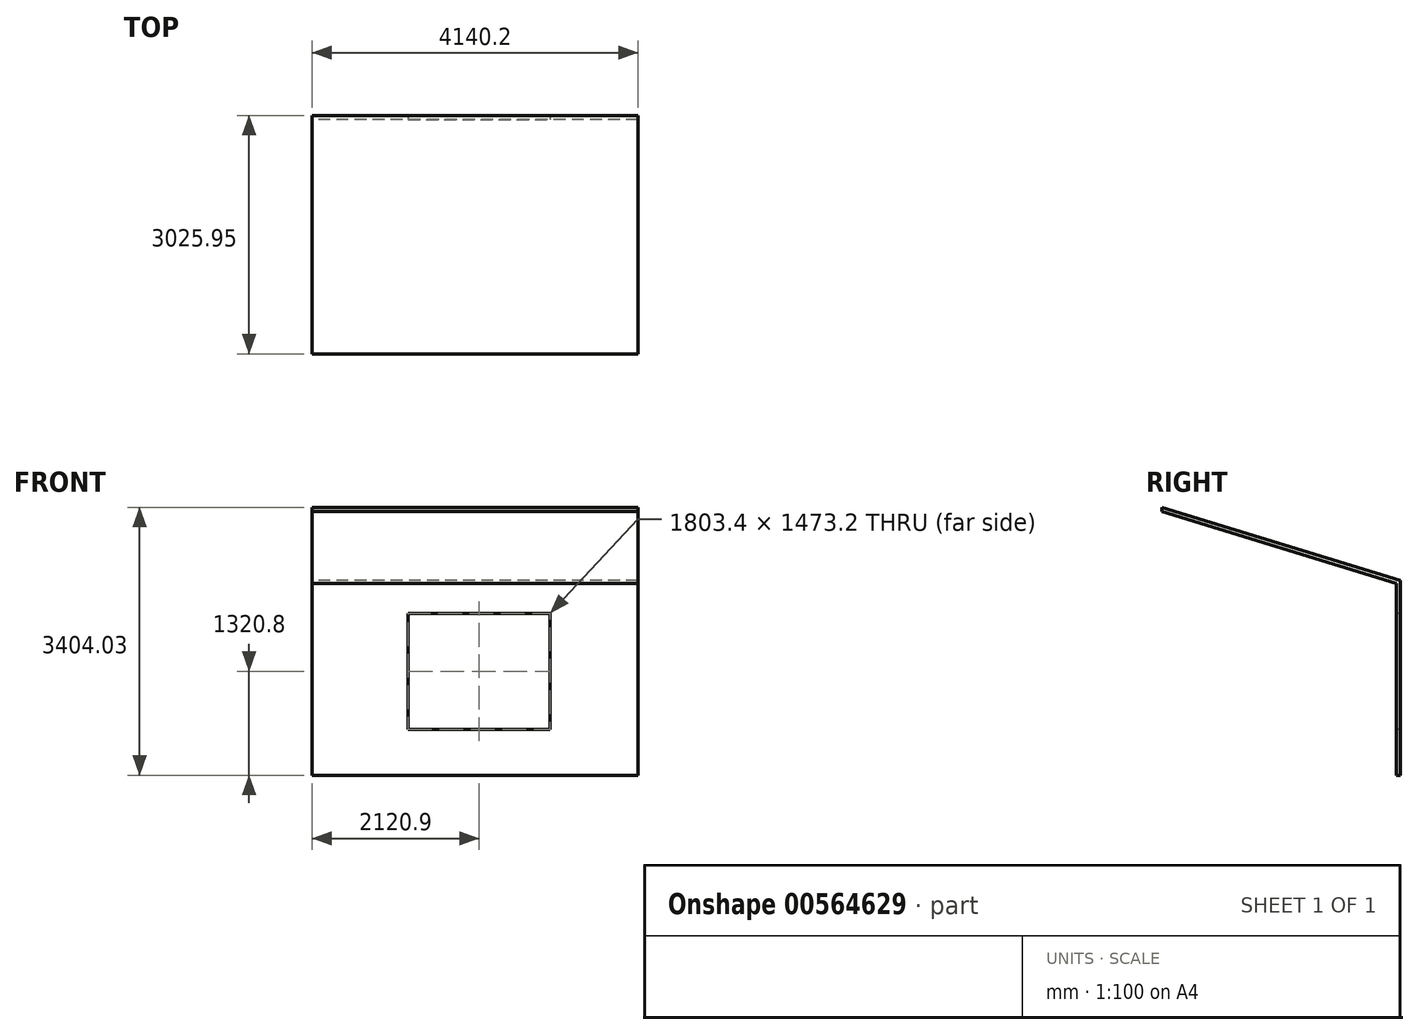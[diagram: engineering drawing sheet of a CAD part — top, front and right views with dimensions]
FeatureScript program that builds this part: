
annotation { "Feature Type Name" : "Feature", "Feature Type Description" : "" }
export const myFeature = defineFeature(function(context is Context, id is Id, definition is map)
    precondition{}
    {
        {
            var Q0;
            Q0=qCreatedBy(makeId("Right.planeOp"),FACE);
            var sketch = newSketch(context, id + "F0", { "sketchPlane" : qUnion([Q0])});
            skLineSegment(sketch, "E0", {"start": v(0, 0) * mm, "end": v(0, 2438.4) * mm});
            skLineSegment(sketch, "E1", {"start": v(0, 2438.4) * mm, "end": v(-2975.15, 3353.23) * mm});
            skLineSegment(sketch, "E2", {"start": v(-2975.15, 3353.23) * mm, "end": v(-2975.15, 3404.03) * mm});
            skLineSegment(sketch, "E3", {"start": v(-2975.15, 3404.03) * mm, "end": v(50.8, 2473.58) * mm});
            skLineSegment(sketch, "E4", {"start": v(50.8, 2473.58) * mm, "end": v(50.8, 0) * mm});
            skLineSegment(sketch, "E5", {"start": v(50.8, 0) * mm, "end": v(0, 0) * mm});
            skSolve(sketch);
        }
        {
            var Q0;
            Q0=makeQuery(id+"F0.imprint","IMPRINT",FACE,{"disambiguationData":[TD([[makeQuery(id+"F0.imprint","IMPRINT",EDGE,{"derivedFrom":sQuery(id+"F0.wireOp",EDGE,"E0")}),-1.0]])]});
            extrude(context, id + "F1", {"entities" : qUnion([Q0]), "depth" : 4140.2 * mm, "offsetDistance" : 25.4 * mm});
        }
        {
            var Q0;
            Q0=makeQuery(id+"F1.opExtrude","SWEPT_FACE",FACE,{"disambiguationData":[OSD([sQuery(id+"F0.wireOp",EDGE,"E0")])]});
            var sketch = newSketch(context, id + "F2", { "sketchPlane" : qUnion([Q0])});
            skLineSegment(sketch, "E6.bottom", {"start": v(1219.2, 2057.4) * mm, "end": v(3022.6, 2057.4) * mm});
            skLineSegment(sketch, "E6.top", {"start": v(1219.2, 584.2) * mm, "end": v(3022.6, 584.2) * mm});
            skLineSegment(sketch, "E6.left", {"start": v(1219.2, 2057.4) * mm, "end": v(1219.2, 584.2) * mm});
            skLineSegment(sketch, "E6.right", {"start": v(3022.6, 2057.4) * mm, "end": v(3022.6, 584.2) * mm});
            skPoint(sketch, "E6.middle", {"position": v(2120.9, 1320.8) * mm});
            skLineSegment(sketch, "E7", {"start": v(3022.6, 584.2) * mm, "end": v(4140.2, 584.2) * mm, "construction": true});
            skLineSegment(sketch, "E8", {"start": v(1219.2, 584.2) * mm, "end": v(0, 584.2) * mm, "construction": true});
            skSolve(sketch);
        }
        {
            var Q0;
            Q0=makeQuery(id+"F2.imprint","IMPRINT",FACE,{"disambiguationData":[TD([[makeQuery(id+"F2.imprint","IMPRINT",EDGE,{"derivedFrom":sQuery(id+"F2.wireOp",EDGE,"E6.bottom")}),-1.0]])]});
            extrude(context, id + "F3", {"entities" : qUnion([Q0]), "operationType" : NewBodyOperationType.REMOVE, "oppositeDirection" : true, "depth" : 127 * mm, "offsetDistance" : 25.4 * mm});
        }
    });
